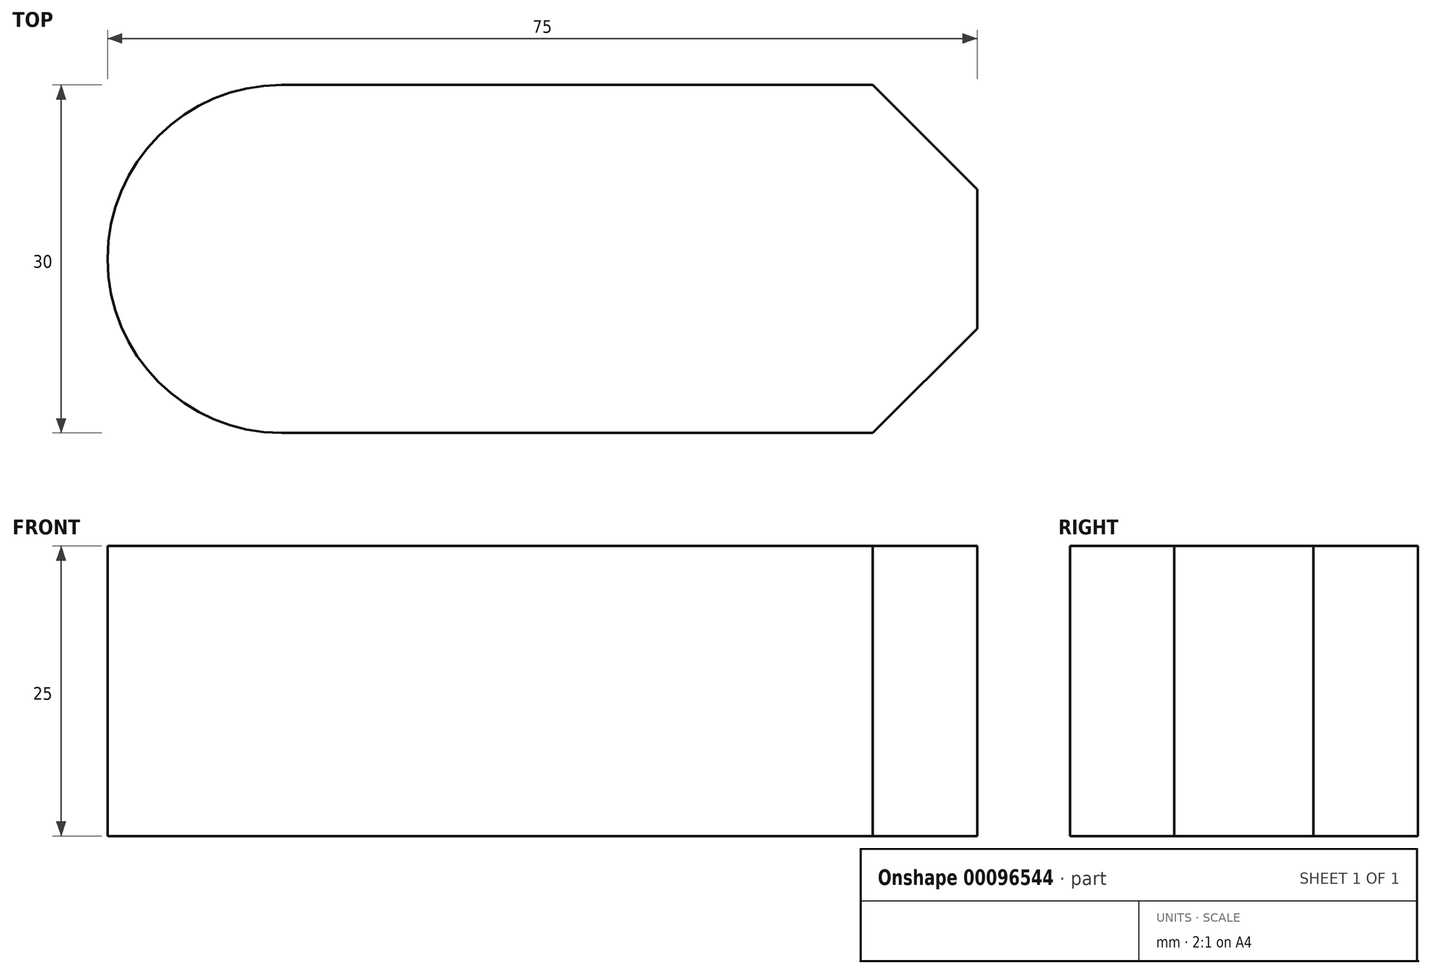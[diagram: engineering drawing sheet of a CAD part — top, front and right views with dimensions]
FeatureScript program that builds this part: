
annotation { "Feature Type Name" : "Feature", "Feature Type Description" : "" }
export const myFeature = defineFeature(function(context is Context, id is Id, definition is map)
    precondition{}
    {
        {
            var Q0;
            Q0=qCreatedBy(makeId("Top.planeOp"),FACE);
            var sketch = newSketch(context, id + "F0", { "sketchPlane" : qUnion([Q0])});
            skLineSegment(sketch, "E0", {"start": v(0, 30) * mm, "end": v(51, 30) * mm});
            skLineSegment(sketch, "E1", {"start": v(51, 0) * mm, "end": v(0, 0) * mm});
            skPoint(sketch, "E2.orphan", {"position": v(61.44, 0) * mm});
            skLineSegment(sketch, "E3", {"start": v(51, 0) * mm, "end": v(60, 9) * mm});
            skLineSegment(sketch, "E4", {"start": v(60, 9) * mm, "end": v(60, 21) * mm});
            skLineSegment(sketch, "E5", {"start": v(60, 21) * mm, "end": v(51, 30) * mm});
            skLineSegment(sketch, "E6.bottom", {"start": v(0, 30) * mm, "end": v(0, 30) * mm});
            skLineSegment(sketch, "E6.top", {"start": v(0, 0) * mm, "end": v(0, 0) * mm});
            skArc(sketch, "E7", {"start": v(0, 30) * mm, "mid": v(-15, 15) * mm, "end": v(0, 0) * mm});
            skSolve(sketch);
        }
        {
            var Q0;
            Q0=makeQuery(id+"F0.imprint","IMPRINT",FACE,{"disambiguationData":[TD([[makeQuery(id+"F0.imprint","IMPRINT",EDGE,{"derivedFrom":sQuery(id+"F0.wireOp",EDGE,"E0")}),-1.0]])]});
            extrude(context, id + "F1", {"entities" : qUnion([Q0]), "depth" : 25 * mm});
        }
    });
